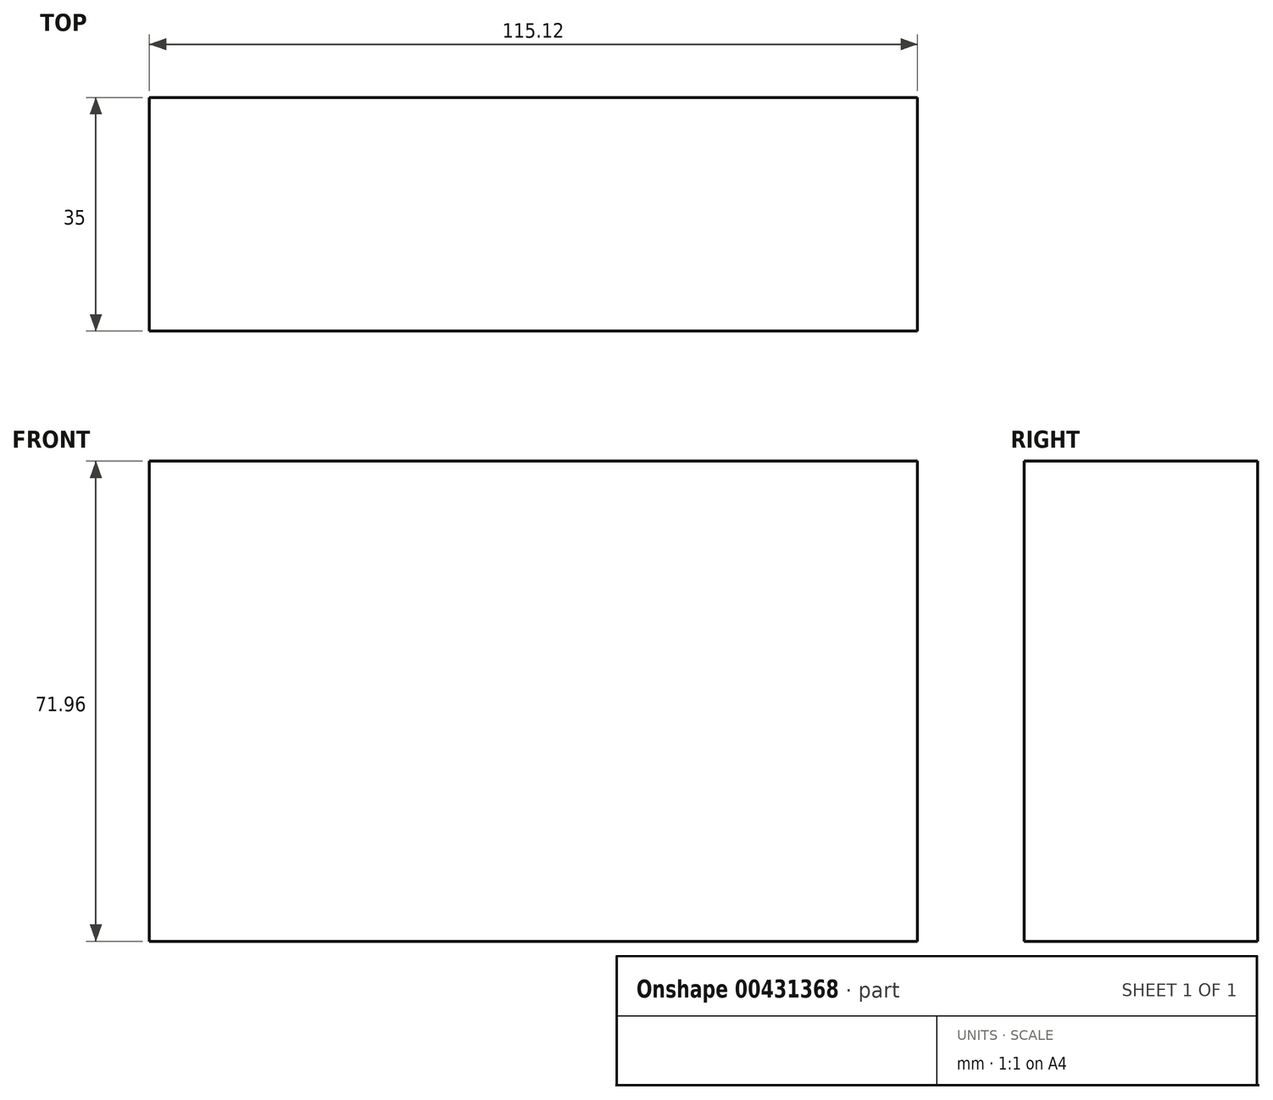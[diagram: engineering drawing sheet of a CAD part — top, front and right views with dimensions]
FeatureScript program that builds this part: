
annotation { "Feature Type Name" : "Feature", "Feature Type Description" : "" }
export const myFeature = defineFeature(function(context is Context, id is Id, definition is map)
    precondition{}
    {
        {
            var Q0;
            Q0=qCreatedBy(makeId("Front.planeOp"),FACE);
            var sketch = newSketch(context, id + "F0", { "sketchPlane" : qUnion([Q0])});
            skLineSegment(sketch, "E0.bottom", {"start": v(57.56, -35.98) * mm, "end": v(-57.56, -35.98) * mm});
            skLineSegment(sketch, "E0.top", {"start": v(57.56, 35.98) * mm, "end": v(-57.56, 35.98) * mm});
            skLineSegment(sketch, "E0.left", {"start": v(57.56, -35.98) * mm, "end": v(57.56, 35.98) * mm});
            skLineSegment(sketch, "E0.right", {"start": v(-57.56, -35.98) * mm, "end": v(-57.56, 35.98) * mm});
            skPoint(sketch, "E0.middle", {"position": v(0, 0) * mm});
            skSolve(sketch);
        }
        {
            var Q0;
            Q0=makeQuery(id+"F0.imprint","IMPRINT",FACE,{"disambiguationData":[TD([[makeQuery(id+"F0.imprint","IMPRINT",EDGE,{"derivedFrom":sQuery(id+"F0.wireOp",EDGE,"E0.bottom")}),-1.0]])]});
            extrude(context, id + "F1", {"entities" : qUnion([Q0]), "depth" : 25 * mm, "hasSecondDirection" : true, "secondDirectionOppositeDirection" : true, "secondDirectionDepth" : 10 * mm});
        }
    });
